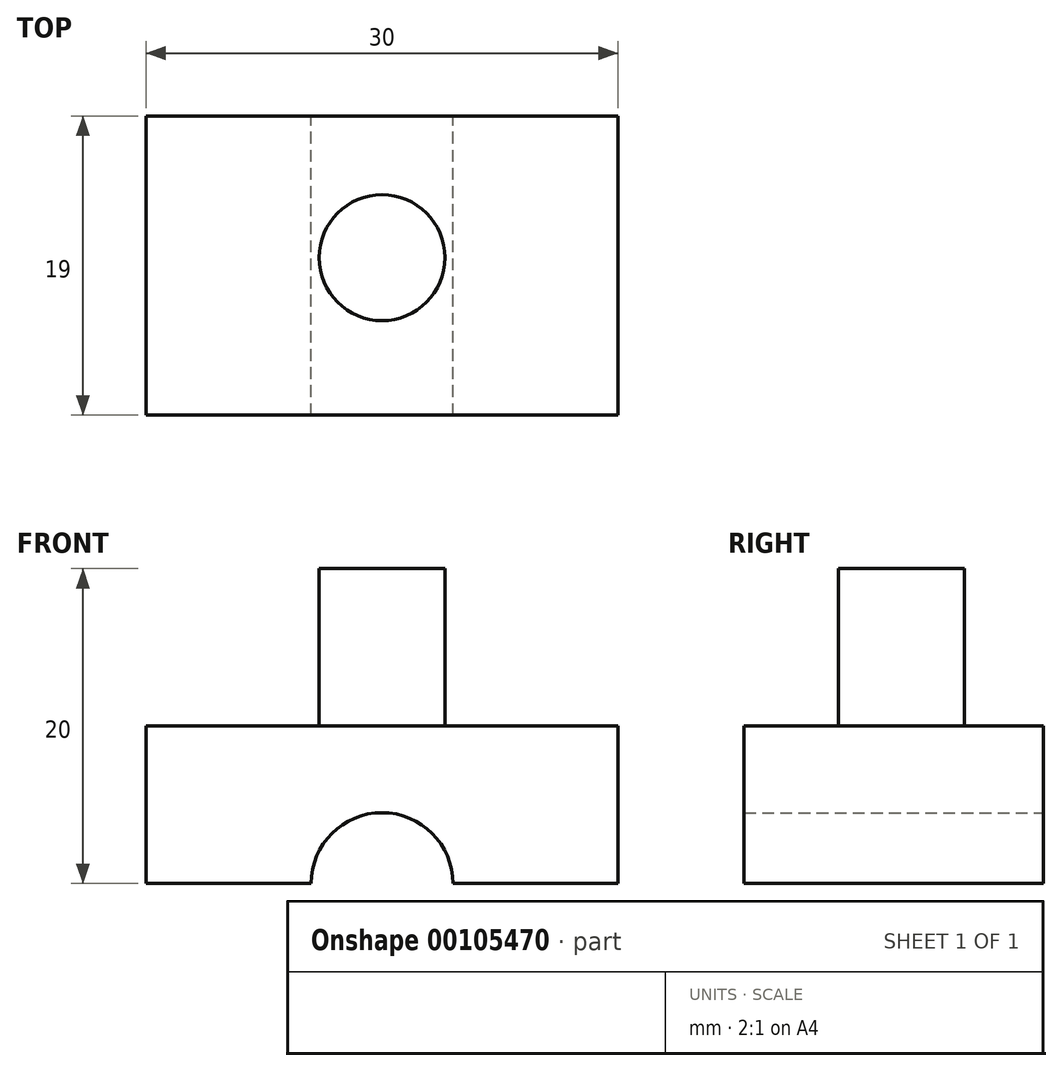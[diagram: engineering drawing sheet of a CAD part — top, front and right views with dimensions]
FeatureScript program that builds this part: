
annotation { "Feature Type Name" : "Feature", "Feature Type Description" : "" }
export const myFeature = defineFeature(function(context is Context, id is Id, definition is map)
    precondition{}
    {
        {
            var Q0;
            Q0=qCreatedBy(makeId("Front.planeOp"),FACE);
            var sketch = newSketch(context, id + "F0", { "sketchPlane" : qUnion([Q0])});
            skLineSegment(sketch, "E0.bottom", {"start": v(-22.47, 10) * mm, "end": v(7.53, 10) * mm});
            skLineSegment(sketch, "E0.top", {"start": v(-22.47, 0) * mm, "end": v(-11.97, 0) * mm});
            skLineSegment(sketch, "E0.left", {"start": v(-22.47, 10) * mm, "end": v(-22.47, 0) * mm});
            skLineSegment(sketch, "E0.right", {"start": v(7.53, 10) * mm, "end": v(7.53, 0) * mm});
            skLineSegment(sketch, "E1", {"start": v(-7.47, 0) * mm, "end": v(-7.47, 0) * mm});
            skArc(sketch, "E2", {"start": v(-2.97, 0) * mm, "mid": v(-7.47, 4.5) * mm, "end": v(-11.97, 0) * mm});
            skLineSegment(sketch, "E3.trimOffspring", {"start": v(-2.97, 0) * mm, "end": v(7.53, 0) * mm});
            skSolve(sketch);
        }
        {
            var Q0;
            Q0 = qSketchRegion(id + "F0", true);
            extrude(context, id + "F1", {"entities" : qUnion([Q0]), "depth" : 19 * mm});
        }
        {
            var Q0;
            Q0=makeQuery(id+"F1.opExtrude","SWEPT_FACE",FACE,{"disambiguationData":[OSD([sQuery(id+"F0.wireOp",EDGE,"E0.bottom")])]});
            var sketch = newSketch(context, id + "F2", { "sketchPlane" : qUnion([Q0])});
            skCircle(sketch, "E4", {"center": v(-7.47, -9) * mm, "radius": 4 * mm});
            skSolve(sketch);
        }
        {
            var Q0;
            Q0 = qSketchRegion(id + "F2", true);
            extrude(context, id + "F3", {"entities" : qUnion([Q0]), "operationType" : NewBodyOperationType.ADD, "depth" : 10 * mm});
        }
    });
